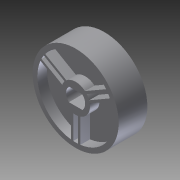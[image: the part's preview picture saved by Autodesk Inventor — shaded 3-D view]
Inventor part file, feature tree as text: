
AUTODESK INVENTOR PART (.ipt)
format: ipt  version: 2012 (Build 160160000, 160)  size: 174,080 bytes
history: native  units: in
note: dims shown in document units (in); Inventor stores cm internally (conversion verified against a paired STEP export)
features: extrude x2, sketch x1
ambient origin geometry x8: Origin, YZ Plane, XZ Plane, XY Plane, X Axis, Y Axis, Z Axis, Center Point
bodies: Solid1 (feature_tree)
feature tree (3):
  sketch  "Sketch1"  dims[d4=0.25in d5=0.3536in d6=0.3536in d7=0.75in d8=2.0in d9=2.25in d10=0.75in d11=0.0in d12=0.25in d13=0.0in d14=0.0625in d15=0.125in d16=0.0625in d17=0.0625in d18=30.0deg d19=1.1811in d21=360.0deg]
  extrude  "Extrusion1"  Depth=0.3536in
  extrude  "Extrusion2"  Depth=0.3536in
